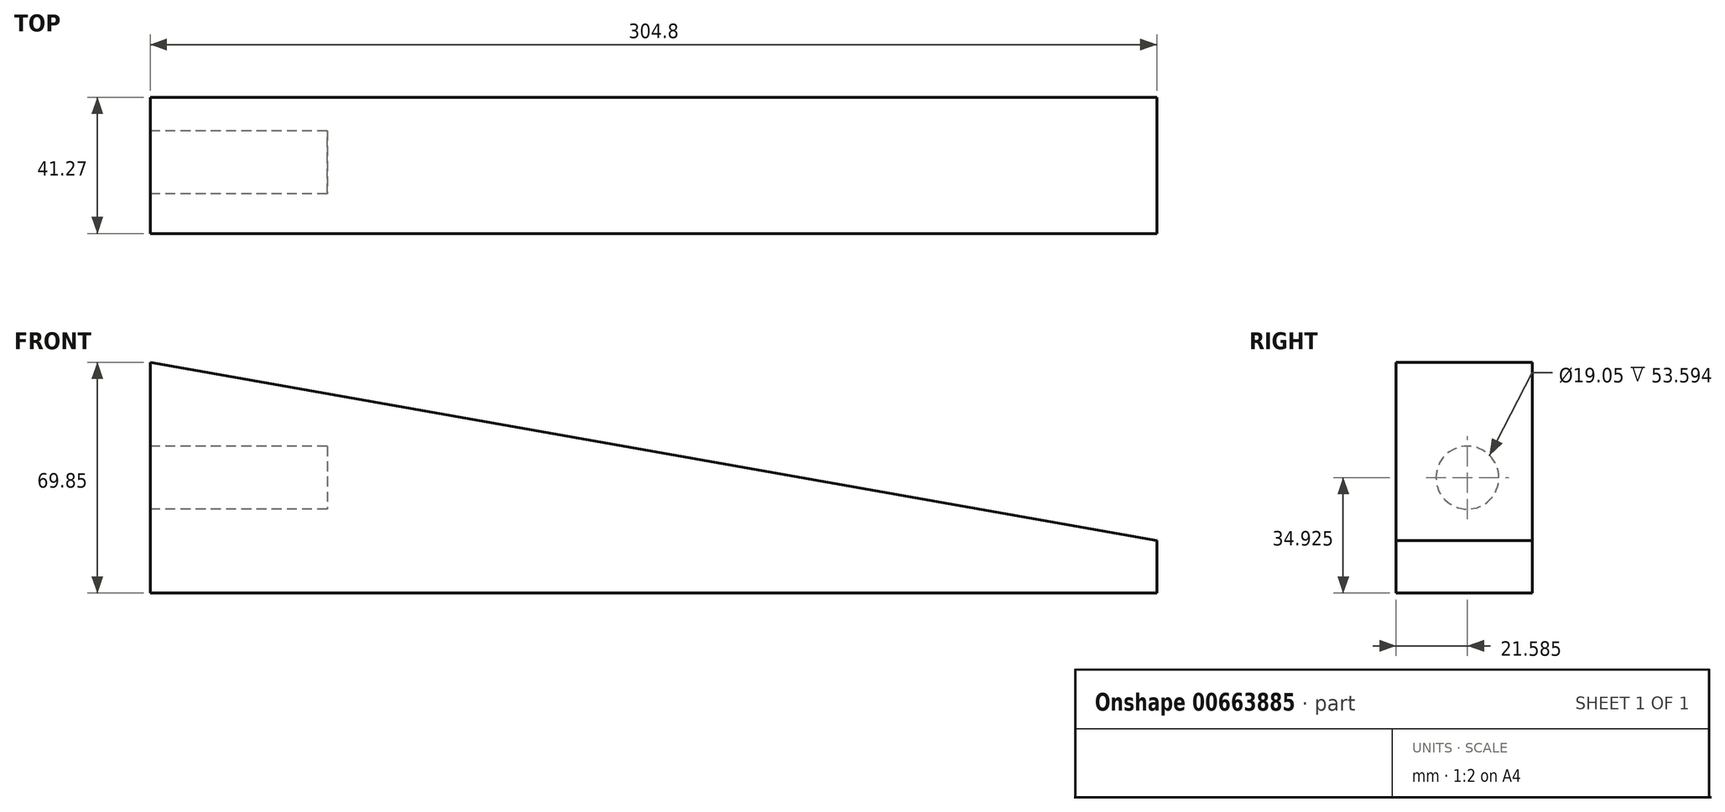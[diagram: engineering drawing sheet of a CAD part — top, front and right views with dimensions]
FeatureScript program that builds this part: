
annotation { "Feature Type Name" : "Feature", "Feature Type Description" : "" }
export const myFeature = defineFeature(function(context is Context, id is Id, definition is map)
    precondition{}
    {
        {
            var Q0;
            Q0=qCreatedBy(makeId("Front.planeOp"),FACE);
            var sketch = newSketch(context, id + "F0", { "sketchPlane" : qUnion([Q0])});
            skLineSegment(sketch, "E0", {"start": v(0, 0) * mm, "end": v(304.8, 0) * mm});
            skLineSegment(sketch, "E1", {"start": v(0, 0) * mm, "end": v(0, 69.85) * mm});
            skLineSegment(sketch, "E2", {"start": v(304.8, 0) * mm, "end": v(304.8, 15.88) * mm});
            skLineSegment(sketch, "E3", {"start": v(0, 69.85) * mm, "end": v(304.8, 15.88) * mm});
            skSolve(sketch);
        }
        {
            var Q0;
            Q0 = qSketchRegion(id + "F0", true);
            extrude(context, id + "F1", {"entities" : qUnion([Q0]), "depth" : 41.27 * mm, "offsetDistance" : 25.4 * mm});
        }
        {
            var Q0;
            Q0=makeQuery(id+"F1.opExtrude","SWEPT_FACE",FACE,{"disambiguationData":[OSD([sQuery(id+"F0.wireOp",EDGE,"E1")])]});
            var sketch = newSketch(context, id + "F2", { "sketchPlane" : qUnion([Q0])});
            skCircle(sketch, "E4", {"center": v(19.69, 34.93) * mm, "radius": 9.53 * mm});
            skSolve(sketch);
        }
        {
            var Q0;
            Q0=makeQuery(id+"F2.imprint","IMPRINT",FACE,{"disambiguationData":[TD([[makeQuery(id+"F2.imprint","IMPRINT",EDGE,{"derivedFrom":sQuery(id+"F2.wireOp",EDGE,"E4")}),1.0]])]});
            extrude(context, id + "F3", {"entities" : qUnion([Q0]), "operationType" : NewBodyOperationType.REMOVE, "oppositeDirection" : true, "depth" : 53.6 * mm, "offsetDistance" : 25.4 * mm});
        }
    });
